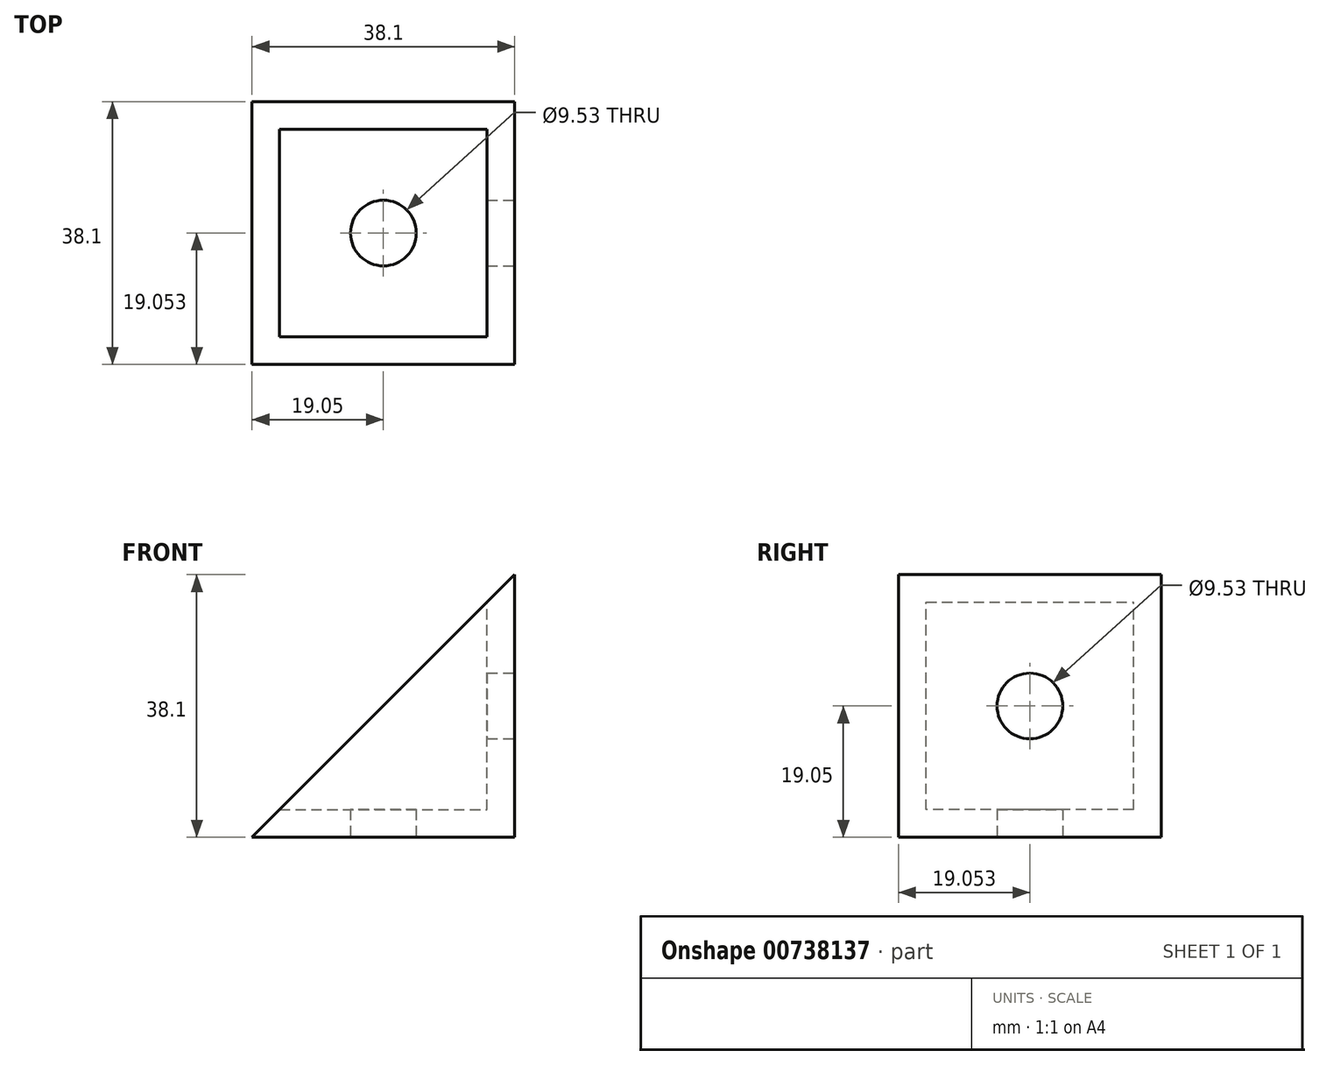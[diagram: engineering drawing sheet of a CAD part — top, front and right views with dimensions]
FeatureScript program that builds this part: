
annotation { "Feature Type Name" : "Feature", "Feature Type Description" : "" }
export const myFeature = defineFeature(function(context is Context, id is Id, definition is map)
    precondition{}
    {
        {
            var Q0;
            Q0=qCreatedBy(makeId("Top.planeOp"),FACE);
            var sketch = newSketch(context, id + "F0", { "sketchPlane" : qUnion([Q0])});
            skLineSegment(sketch, "E0.bottom", {"start": v(-14.22, 22.06) * mm, "end": v(23.88, 22.06) * mm});
            skLineSegment(sketch, "E0.top", {"start": v(-14.22, -16.04) * mm, "end": v(23.88, -16.04) * mm});
            skLineSegment(sketch, "E0.left", {"start": v(-14.22, 22.06) * mm, "end": v(-14.22, -16.04) * mm});
            skLineSegment(sketch, "E0.right", {"start": v(23.88, 22.06) * mm, "end": v(23.88, -16.04) * mm});
            skCircle(sketch, "E1", {"center": v(4.83, 3.01) * mm, "radius": 4.76 * mm});
            skLineSegment(sketch, "E2", {"start": v(4.83, 3.01) * mm, "end": v(-14.22, 3.01) * mm});
            skSolve(sketch);
        }
        {
            var Q0;
            Q0=makeQuery(id+"F0.imprint","IMPRINT",FACE,{"disambiguationData":[TD([[makeQuery(id+"F0.imprint","IMPRINT",EDGE,{"derivedFrom":sQuery(id+"F0.wireOp",EDGE,"E0.bottom")}),-1.0]])]});
            extrude(context, id + "F1", {"entities" : qUnion([Q0]), "depth" : 38.1 * mm, "offsetDistance" : 25 * mm});
        }
        {
            var Q0;
            Q0=makeQuery(id+"F1.opExtrude","SWEPT_FACE",FACE,{"disambiguationData":[OSD([sQuery(id+"F0.wireOp",EDGE,"E0.right")])]});
            var sketch = newSketch(context, id + "F2", { "sketchPlane" : qUnion([Q0])});
            skCircle(sketch, "E3", {"center": v(3.01, 19.05) * mm, "radius": 4.76 * mm});
            skLineSegment(sketch, "E4", {"start": v(3.01, 19.05) * mm, "end": v(-16.04, 19.05) * mm});
            skSolve(sketch);
        }
        {
            var Q0;
            Q0=makeQuery(id+"F2.imprint","IMPRINT",FACE,{"disambiguationData":[TD([[makeQuery(id+"F2.imprint","IMPRINT",EDGE,{"derivedFrom":sQuery(id+"F2.wireOp",EDGE,"E3")}),1.0]])]});
            extrude(context, id + "F3", {"entities" : qUnion([Q0]), "operationType" : NewBodyOperationType.REMOVE, "oppositeDirection" : true, "depth" : 25 * mm, "offsetDistance" : 25 * mm});
        }
        {
            var Q0;
            Q0=makeQuery(id+"F1.opExtrude","SWEPT_FACE",FACE,{"disambiguationData":[OSD([sQuery(id+"F0.wireOp",EDGE,"E0.top")])]});
            var sketch = newSketch(context, id + "F4", { "sketchPlane" : qUnion([Q0])});
            skLineSegment(sketch, "E5", {"start": v(23.88, 38.1) * mm, "end": v(-14.22, 0) * mm});
            skSolve(sketch);
        }
        {
            var Q0;
            Q0=makeQuery(id+"F1.opExtrude","CAP_FACE",FACE,{"disambiguationData":[OSD([sQuery(id+"F0.wireOp",EDGE,"E0.bottom"),sQuery(id+"F0.wireOp",EDGE,"E0.top"),sQuery(id+"F0.wireOp",EDGE,"E0.left"),sQuery(id+"F0.wireOp",EDGE,"E0.right"),sQuery(id+"F0.wireOp",EDGE,"E1")])],"isStart":false});
            var sketch = newSketch(context, id + "F5", { "sketchPlane" : qUnion([Q0])});
            skLineSegment(sketch, "E6.top", {"start": v(4.83, 18.06) * mm, "end": v(-10.22, 18.06) * mm});
            skLineSegment(sketch, "E6.right", {"start": v(-10.22, 3.01) * mm, "end": v(-10.22, 18.06) * mm});
            skPoint(sketch, "E6.bottom.start.orphan", {"position": v(4.83, 3.01) * mm});
            skLineSegment(sketch, "E7", {"start": v(4.83, 18.06) * mm, "end": v(4.83, 10.5) * mm});
            skLineSegment(sketch, "E8.MirrorCS", {"start": v(19.88, 3.01) * mm, "end": v(19.88, 18.06) * mm});
            skLineSegment(sketch, "E9.MirrorCS", {"start": v(4.83, 18.06) * mm, "end": v(19.88, 18.06) * mm});
            skLineSegment(sketch, "E10", {"start": v(19.88, 3.01) * mm, "end": v(15, 3.01) * mm});
            skLineSegment(sketch, "E11.MirrorCS", {"start": v(19.88, 3.01) * mm, "end": v(19.88, -12.04) * mm});
            skLineSegment(sketch, "E12.MirrorCS", {"start": v(4.83, -12.04) * mm, "end": v(19.88, -12.04) * mm});
            skLineSegment(sketch, "E13.MirrorCS", {"start": v(4.83, -12.04) * mm, "end": v(-10.22, -12.04) * mm});
            skLineSegment(sketch, "E14.MirrorCS", {"start": v(-10.22, 3.01) * mm, "end": v(-10.22, -12.04) * mm});
            skSolve(sketch);
        }
        {
            var Q0;
            Q0=makeQuery(id+"F5.imprint","IMPRINT",FACE,{"disambiguationData":[TD([[makeQuery(id+"F5.imprint","IMPRINT",EDGE,{"derivedFrom":sQuery(id+"F5.wireOp",EDGE,"E6.top")}),1.0]])]});
            extrude(context, id + "F6", {"entities" : qUnion([Q0]), "operationType" : NewBodyOperationType.REMOVE, "oppositeDirection" : true, "depth" : 34.1 * mm, "offsetDistance" : 25 * mm});
        }
        {
            var Q0;
            Q0=makeQuery(id+"F1.opExtrude","SWEPT_FACE",FACE,{"disambiguationData":[OSD([sQuery(id+"F0.wireOp",EDGE,"E0.left")])]});
            var sketch = newSketch(context, id + "F7", { "sketchPlane" : qUnion([Q0])});
            skLineSegment(sketch, "E15.top", {"start": v(-3.01, 34.1) * mm, "end": v(-18.06, 34.1) * mm});
            skLineSegment(sketch, "E15.right", {"start": v(-18.06, 19.05) * mm, "end": v(-18.06, 34.1) * mm});
            skLineSegment(sketch, "E16", {"start": v(-3.01, 34.1) * mm, "end": v(-3.01, 27.9) * mm});
            skLineSegment(sketch, "E17.MirrorCS", {"start": v(12.04, 19.05) * mm, "end": v(12.04, 34.1) * mm});
            skLineSegment(sketch, "E18.MirrorCS", {"start": v(-3.01, 34.1) * mm, "end": v(12.04, 34.1) * mm});
            skLineSegment(sketch, "E19", {"start": v(12.04, 19.05) * mm, "end": v(5.76, 19.05) * mm});
            skLineSegment(sketch, "E20.MirrorCS", {"start": v(-3.01, 4) * mm, "end": v(12.04, 4) * mm});
            skLineSegment(sketch, "E21.MirrorCS", {"start": v(12.04, 19.05) * mm, "end": v(12.04, 4) * mm});
            skLineSegment(sketch, "E22.MirrorCS", {"start": v(-3.01, 4) * mm, "end": v(-18.06, 4) * mm});
            skLineSegment(sketch, "E23.MirrorCS", {"start": v(-18.06, 19.05) * mm, "end": v(-18.06, 4) * mm});
            skSolve(sketch);
        }
        {
            var Q0;
            Q0=makeQuery(id+"F7.imprint","IMPRINT",FACE,{"disambiguationData":[TD([[makeQuery(id+"F7.imprint","IMPRINT",EDGE,{"derivedFrom":sQuery(id+"F7.wireOp",EDGE,"E15.top")}),1.0]])]});
            extrude(context, id + "F8", {"entities" : qUnion([Q0]), "operationType" : NewBodyOperationType.REMOVE, "oppositeDirection" : true, "depth" : 34.1 * mm, "offsetDistance" : 25 * mm});
        }
        {
            var Q0;
            Q0=makeQuery(id+"F4.imprint","IMPRINT",FACE,{"disambiguationData":[TD([[makeQuery(id+"F4.imprint","IMPRINT",EDGE,{"derivedFrom":sQuery(id+"F4.wireOp",EDGE,"E5")}),-1.0]])]});
            extrude(context, id + "F9", {"entities" : qUnion([Q0]), "operationType" : NewBodyOperationType.REMOVE, "oppositeDirection" : true, "depth" : 50 * mm, "offsetDistance" : 25 * mm});
        }
    });
